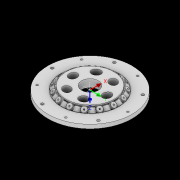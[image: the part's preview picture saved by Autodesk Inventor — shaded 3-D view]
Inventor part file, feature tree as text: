
AUTODESK INVENTOR PART (.ipt)
format: ipt  version: 2022.2 (Build 262287010, 287A)  size: 1,376,256 bytes
history: native  units: mm
features: other x27, extrude x26, sketch x16, pattern_circular x10, plane x4, fillet x2, move_body x2, revolve x2, draft x2, chamfer x2
ambient origin geometry x8: Origin, YZ Plane, XZ Plane, XY Plane, X Axis, Y Axis, Z Axis, Center Point
bodies: Solid5 (feature_tree)
feature tree (93):
  other  "CrossSection1"
  sketch  "Sketch7"  dims[d167=8.972256mm]
  other  "Roller1"
  other  "Roller2"
  sketch  "Sketch22"  dims[d173=10.814812mm d201=60.0mm]
  sketch  "Sketch2"  dims[d57=4.025mm d90=38.448826mm]
  sketch  "Sketch23"  dims[d232=0.0mm d233=3600.0mm d343=16.433653mm d344=16.419189mm]
  other  "RevRoller1"
  fillet  "Fillet1"  Radius=35.755189mm
  extrude  "Extrusion39"  Depth=38.448826mm
  pattern_circular  "Circular Pattern13"  Count=6  [1 undecoded]
  move_body  "Move Body7"
  revolve  "Revolution13"  [1 undecoded]
  fillet  "Fillet3"  Radius=16.419189mm
  pattern_circular  "Circular Pattern14"  [2 undecoded]
  move_body  "Move Body6"
  revolve  "Revolution14"  [1 undecoded]
  other  "OuterRim_Top2"
  other  "OuterRim_Bottom2"
  plane  "Work Plane8"
  sketch  "Sketch49"  dims[d352=0.025mm]
  sketch  "Sketch50"  dims[d354=0.025mm]
  sketch  "Sketch51"  dims[d355=16.433653mm]
  extrude  "Extrusion40"  TaperAngle=360.0deg  [1 undecoded]
  extrude  "Extrusion41"  Depth=0.5mm
  extrude  "Extrusion42"  Depth=0.5mm
  extrude  "Extrusion43"  Depth=0.5mm
  sketch  "Sketch52"  dims[d356=16.419189mm]
  extrude  "Extrusion44"  Depth=0.5mm
  extrude  "Extrusion45"  Depth=0.5mm
  extrude  "Extrusion46"  TaperAngle=90.0deg  [1 undecoded]
  extrude  "Extrusion47"  Depth=0.5mm
  pattern_circular  "Circular Pattern32"  Count=15  [1 undecoded]
  pattern_circular  "Circular Pattern33"  Angle=360.0deg  [1 undecoded]
  sketch  "Sketch57"  dims[d358=360.0deg d359=0.5mm d360=150.0mm d361=360.0deg d363=2.094395mm d367=8.1mm d370=0.025mm d371=1.0mm d372=2.094395mm d373=90.0deg d374=0.5mm d375=150.0mm d376=360.0deg d378=90.0deg d379=0.1mm d380=0.025mm d381=0.025mm d382=0.025mm d383=0.025mm d384=11.040614mm d385=0.0mm d386=0.0mm d391=12.0mm d392=60.0mm d393=1.5mm d394=1.5mm d395=1.5mm d396=1.5mm d397=90.0deg d398=90.0deg d399=90.0deg d400=60.0mm d401=11.040614mm d402=0.0mm d486=0.436332mm d487=0.5mm d488=2.0mm d489=0.0mm d490=20.0mm d495=2.5mm d496=8.0mm d506=13.856406mm d507=55.5mm d508=8.0mm d509=0.05mm d510=2.5mm d511=30.0deg d512=12.0mm d513=6.0mm d514=0.2mm d515=30.0deg d516=131.0mm d517=65.5mm d518=0.2mm d519=100.0mm d520=120.0mm d521=2.0mm d522=150.0mm d530=50.0mm d531=5.5mm d532=5.5mm d533=5.5mm d534=85.75mm d535=73.5mm d536=61.25mm d537=24.5mm d538=3.0mm d539=2.4mm d540=0.0mm d541=0.0mm d542=0.0mm d543=5.5mm d544=3.0mm d545=0.0mm d546=90.0mm d547=360.0deg d549=3.0mm d550=3.0mm d551=2.4mm d552=0.0mm d553=5.520307mm d554=0.0mm d555=2.4mm d556=0.0mm d557=5.520307mm d558=0.0mm d559=5.520307mm d560=0.0mm d561=90.0mm d562=360.0deg d564=60.0mm d565=360.0deg d567=5.5mm d568=5.5mm d569=3.0mm d570=0.0mm d571=5.520307mm d572=0.0mm d573=3.0mm d574=0.0mm d575=5.520307mm d576=0.0mm d577=90.0mm d578=360.0deg d580=60.0mm d581=360.0deg d584=20.0mm d585=8.0mm d587=1.75mm d589=3.0mm d592=2.0mm d593=12.0mm d594=12.0mm d600=0.5mm d601=2.0mm d602=45.0deg d603=0.5mm d604=2.0mm d605=45.0deg d606=0.436332mm d607=0.5mm d608=0.0mm d609=20.0mm d611=360.0deg d613=0.0mm d614=0.0mm d617=0.99971mm d618=100.0mm d620=54.0mm d621=5.0mm d622=0.5mm d623=0.5mm d624=5.0mm d625=0.2mm d626=0.0mm d627=20.0mm d629=54.0mm d630=48.5mm d631=20.0mm d633=6.283185mm d635=5.5mm d636=3.0mm d637=7.0mm d638=4.0mm d639=5.520307mm d640=0.0mm d641=3.0mm d642=0.0mm d643=5.520307mm d644=0.0mm d645=4.0mm d646=0.0mm d647=20.0mm d649=6.283185mm d651=3.0mm d652=4.0mm d653=20.0mm d655=6.283185mm d657=7.0mm d658=5.5mm d659=5.520307mm d660=0.0mm d661=2.440614mm d662=0.0mm d663=5.520307mm d664=0.0mm d665=3.040614mm d666=0.0mm d679=50.0mm d680=360.0deg d682=50.0mm d683=360.0deg d694=6.35mm d695=6.35mm d696=6.4mm d697=5.45mm d698=11.194mm d699=0.0mm d700=8.194mm d701=0.0mm d702=60.0mm d703=360.0deg d705=0.0mm d706=0.0mm d707=0.0mm d708=0.0mm d709=0.0mm d710=0.0mm d16=0.872665mm d17=0.872665mm d49=0.872665mm d50=0.872665mm d51=0.872665mm d52=0.872665mm d236=0.5mm d237=0.872665mm d238=0.5mm d239=0.872665mm d282=1.0mm d283=1.0mm d284=1.0mm d285=0.15mm d286=0.25mm d287=0.375mm d288=14.3117mm d289=0.75mm d290=20.594885mm d291=0.0625mm d292=0.75mm d293=0.375mm d405=0.5mm d406=0.872665mm d407=0.5mm d408=0.872665mm d413=0.5mm d414=0.872665mm d415=0.5mm d416=0.872665mm d417=0.5mm d418=0.872665mm d419=0.5mm d420=0.872665mm d421=0.872665mm d431=0.5mm d432=0.872665mm d433=0.5mm d434=0.872665mm d471=0.5mm d472=0.872665mm d473=0.5mm d474=0.872665mm d497=0.5mm d498=0.872665mm d499=0.5mm d500=0.872665mm d590=0.5mm d591=0.872665mm]
  extrude  "Extrusion50"  TaperAngle=90.0deg  [1 undecoded]
  extrude  "Extrusion51"  Depth=0.1mm
  pattern_circular  "Circular Pattern34"  [2 undecoded]
  other  "UCS1"
  plane  "Work Plane7"
  sketch  "Sketch47"  dims[d350=47.84958mm]
  extrude  "Rotor_Ring"  Depth=0.5mm
  draft  "FaceDraft2"
  sketch  "Sketch30"  dims[d345=0.025mm]
  plane  "Work Plane5"
  other  "Rotor Featurs"
  other  "RotorRim_Bottom"
  extrude  "Extrusion24"  Depth=0.5mm
  extrude  "Extrusion25"  Depth=0.5mm
  extrude  "Extrusion26"  Depth=11.040614mm
  pattern_circular  "Circular Pattern23"  [2 undecoded]
  sketch  "Sketch41"  dims[d347=0.1mm]
  extrude  "Extrusion27"  TaperAngle=0.0deg  [1 undecoded]
  extrude  "Extrusion28"  Depth=12.0mm
  pattern_circular  "Circular Pattern24"  Count=6  [1 undecoded]
  extrude  "Extrusion29"  Depth=0.5mm
  extrude  "Extrusion30"  Depth=0.5mm
  extrude  "Extrusion31"  Depth=0.5mm
  pattern_circular  "Circular Pattern25"  [2 undecoded]
  sketch  "Sketch42"  dims[d348=0.1mm]
  extrude  "Extrusion32"  TaperAngle=90.0deg  [1 undecoded]
  extrude  "Extrusion33"  TaperAngle=90.0deg  [1 undecoded]
  extrude  "Extrusion34"  TaperAngle=90.0deg  [1 undecoded]
  extrude  "Extrusion35"  Depth=0.5mm
  pattern_circular  "Circular Pattern26"  [2 undecoded]
  pattern_circular  "Circular Pattern27"  [2 undecoded]
  chamfer  "Chamfer1"  Distance=0.436332mm
  chamfer  "Chamfer2"  Distance=0.5mm
  draft  "FaceDraft4"
  plane  "Work Plane6"
  sketch  "Sketch43"  dims[d349=47.835115mm]
  extrude  "Extrusion37"  Depth=0.5mm
  extrude  "Extrusion38"  Depth=8.0mm
  other  "2D Equation Curve1"
  sketch  "Sketch40"  dims[d346=0.025mm]
  other  "Work Axis6"
  other  "Work Axis7"
  other  "Work Axis8"
  other  "Work Axis9"
  other  "Work Axis10"
  other  "Work Point1"
  other  "Work Point2"
  other  "Work Point3"
  other  "Work Point4"
  other  "Work Point5"
  sketch  "Sketch48"  dims[d351=0.025mm]
  other  "UCS1: YZ Plane"
  other  "UCS1: XZ Plane"
  other  "UCS1: XY Plane"
  other  "UCS1: X Axis"
  other  "UCS1: Y Axis"
  other  "UCS1: Z Axis"
  other  "UCS1: Center Point"
note: 25 required parameter values undecoded (feature->parameter linkage not recoverable at this tier; creation-order binding heuristic only, values carry confidence <= 0.55)